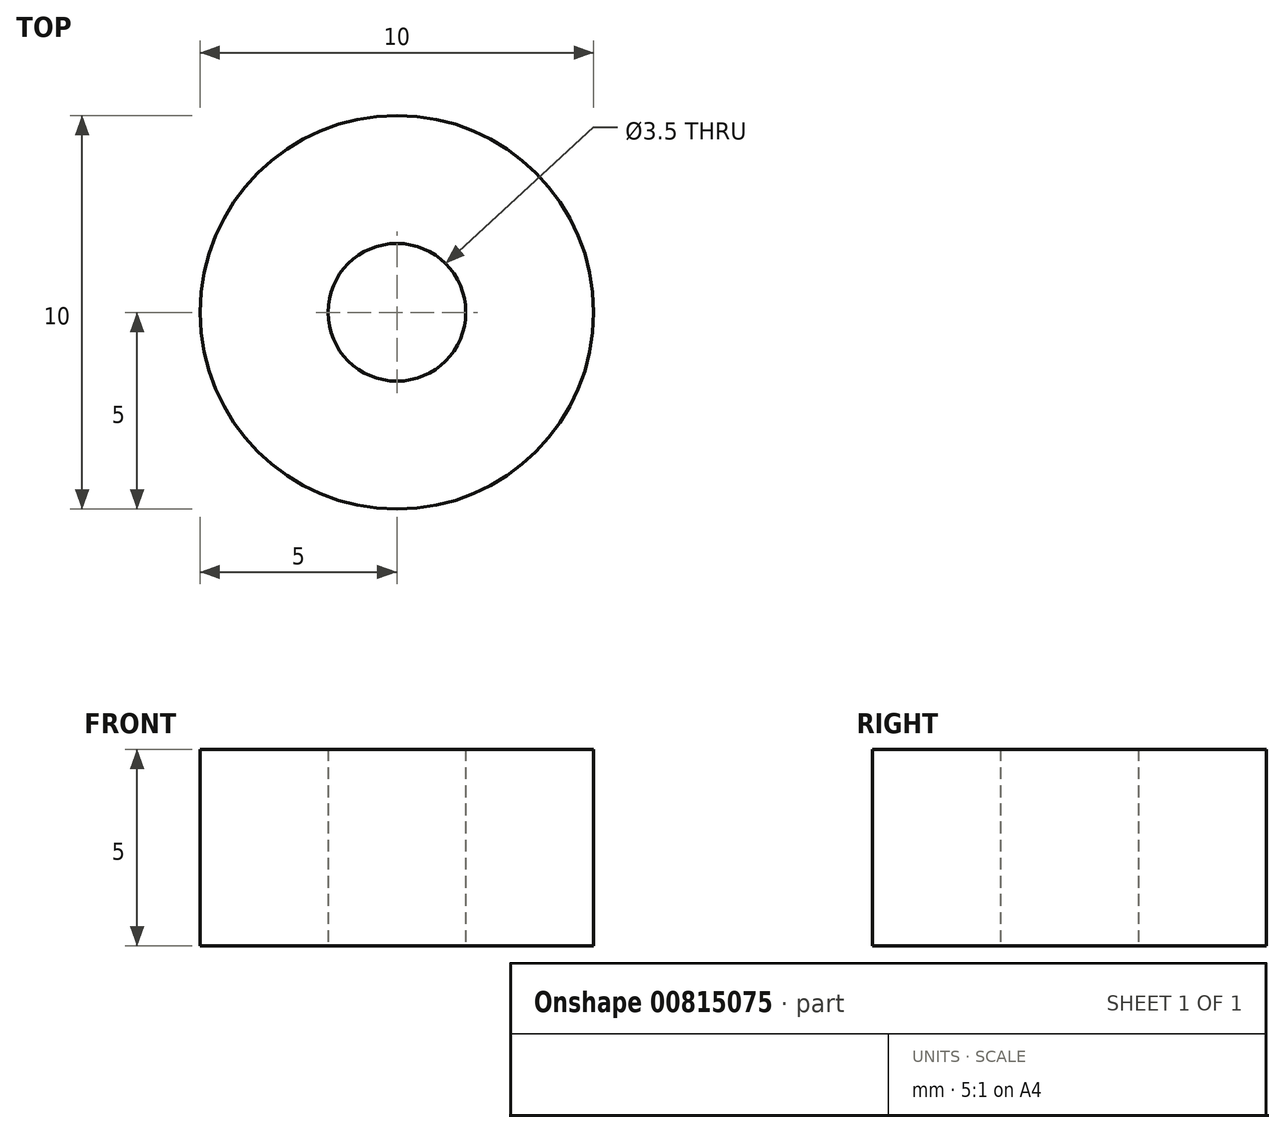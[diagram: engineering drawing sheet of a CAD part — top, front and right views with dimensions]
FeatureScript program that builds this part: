
annotation { "Feature Type Name" : "Feature", "Feature Type Description" : "" }
export const myFeature = defineFeature(function(context is Context, id is Id, definition is map)
    precondition{}
    {
        {
            var Q0;
            Q0=qCreatedBy(makeId("Top.planeOp"),FACE);
            var sketch = newSketch(context, id + "F0", { "sketchPlane" : qUnion([Q0])});
            skCircle(sketch, "E0", {"center": v(0, 0) * mm, "radius": 5 * mm});
            skCircle(sketch, "E1", {"center": v(0, 0) * mm, "radius": 1.75 * mm});
            skCircle(sketch, "E2", {"center": v(0, 0) * mm, "radius": 3.5 * mm});
            skSolve(sketch);
        }
        {
            var Q0;
            Q0=makeQuery(id+"F0.imprint","IMPRINT",FACE,{"disambiguationData":[TD([[makeQuery(id+"F0.imprint","IMPRINT",EDGE,{"derivedFrom":sQuery(id+"F0.wireOp",EDGE,"E1")}),-1.0]])]});
            var Q1;
            Q1=makeQuery(id+"F0.imprint","IMPRINT",FACE,{"disambiguationData":[TD([[makeQuery(id+"F0.imprint","IMPRINT",EDGE,{"derivedFrom":sQuery(id+"F0.wireOp",EDGE,"E0")}),1.0]])]});
            extrude(context, id + "F1", {"entities" : qUnion([Q0, Q1]), "depth" : 5 * mm, "offsetDistance" : 25 * mm});
        }
    });
